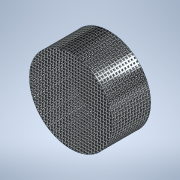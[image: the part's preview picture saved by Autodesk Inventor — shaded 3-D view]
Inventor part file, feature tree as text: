
AUTODESK INVENTOR PART (.ipt)
format: ipt  version: 2020 (Build 240168000, 168)  size: 128,512 bytes
history: native  units: mm
features: extrude x1, sketch x1
ambient origin geometry x8: Origin, YZ Plane, XZ Plane, XY Plane, X Axis, Y Axis, Z Axis, Center Point
bodies: Solid1 (feature_tree)
feature tree (2):
  extrude  "Extrusion1"  Depth=35.0mm TaperAngle=0.0deg
  sketch  "Sketch1"  dims[d0=75.0mm d1=35.0mm d2=0.0mm]
